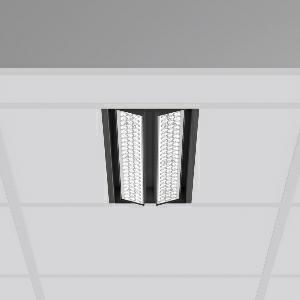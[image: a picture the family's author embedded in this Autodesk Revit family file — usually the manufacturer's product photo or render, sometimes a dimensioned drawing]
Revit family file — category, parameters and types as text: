
# Revit family: tx-move_901736_003_76_b229
name_source: partatom
category: Lighting Fixtures
units: mm (PartAtom-declared; Revit-internal decimal feet)

## family parameters
Cut with Voids When Loaded = No
Host = Face
Light Source = No
Part Type = Normal
Room Calculation Point = No
Round Connector Dimension = Use Diameter
Shared = No

## types (1)
- MultiLumen 1 (1 x LED Modul 830, 2750 lm, 3000)
    Apparent Load = 35 VA
    Approval mark = CE
    CIE Flux Codes = 90 97 99 100 100
    Color Rendering = 80
    Color Temperature = 3000
    Default Elevation = 1800 mm
    Description = Series: TX-MOVE
Einlege/Einbau-Flächenstrahler. Housing: sheet steel, powder-coated. 2xSwivel range: 90°. High-efficiency LED units with optimum light control thanks to clear plastic (PC) lens optics. Spezielle Mikrostrukturen reduzieren Gelbsaum. Symmetrical light distribution. Suitable for laying in grid ceiling module 625. Connected converter included in separate gearbox.Suitable for through-wiring.MultiLumen: Luminous flux adjustable in 3 steps. Accessories: Mounting frame for installation in suspended ceilings. Environmentally friendly and resource-saving due to replaceable and recyclable components. 
Colour: deep black, matt (RAL 9005)
Length: 622 mm
Width: 190 mm
Height: 39 mm
Cut-out length: 602 mm
Cut-out width: 174 mm
Recess height: 100 mm
Lamp: LED
Socket: without socket
Colour temperature: 3000K
Colour rendering index (CRI): 80
System power: 35 W
Rated luminous flux: 5500 lm
Luminous efficiency: 157 lm/W
System power 2: 47 W
Rated luminous flux 2: 7100 lm
Luminous efficiency 2: 151 lm/W
System power 3: 68 W
Rated luminous flux 3: 9700 lm
Luminous efficiency 3: 143 lm/W
Control gear: Dimmable EVG, DALI
Protection class: I
Type of protection: IP 20
    Height = 0 mm  [stored 0 ft]
    Lamp = 1 x LED Modul 830
    Lamp Light Flux = 2750 lm
    Lamp count = 1
    Length = 622 mm
    Lifetime = 50000 h
    Luminous efficacy = 157 lm/W
    Manufacturer = RZB
    ModVariant = No
    Model = 901736.003.76
    Mounting Place = Ceiling, Wall
    Mounting Type = Recessed
    Number of Poles = 1
    OnlyDefault = Yes
    Power Factor = 1
    Product Name = TX-MOVE
    Product group = Recessed projectors
    ProductGroupID = 401
    Protection Class = Protection class I
    Protection Degree = IP 20
    RLX_Detail_Level = 1
    RLX_Emergency_Light_Flux = 0 lm
    RLX_Emergency_Type = 0
    RLX_Emergency_Type_DB = No
    RlxData = <blob elided: 35773 chars, md5=66d9085f>
    Socket = socket
    Standby Power = 0 W
    System Light Flux = 5500 lm
    System Power = 35 W
    Type Comments = MultiLumen 1
    Type Image = 901737.003.jpg
    URL = http://relux.com
    VarID = multilumen_1
    Voltage = 230 V
    Voltage Range = 220-240 V
    Weight = 0.00 kg
    Width = 190 mm  [stored 0.62336 ft]

note: [stored X ft] marks values corroborated as IEEE doubles in the binary element streams (Revit-internal decimal feet)

## geometry (parser evidence)
native form markers: Blend x4, Sweep x15
no freeform markers — native parametric forms only
